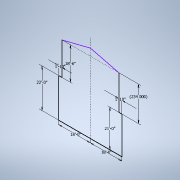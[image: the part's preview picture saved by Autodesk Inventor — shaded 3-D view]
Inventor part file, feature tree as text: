
AUTODESK INVENTOR PART (.ipt)
format: ipt  version: 2020.1 (Build 241239000, 239)  size: 94,720 bytes
history: native  units: in
note: dims shown in document units (in); Inventor stores cm internally (conversion verified against a paired STEP export)
features: sketch x1
ambient origin geometry x8: Origin, YZ Plane, XZ Plane, XY Plane, X Axis, Y Axis, Z Axis, Center Point
feature tree (1):
  sketch  "Sketch1"  dims[d0=216.0in d1=216.0in d2=22.0in d3=222.0in d4=264.0in d5=252.0in d6=22.0in d10=234.0in]
